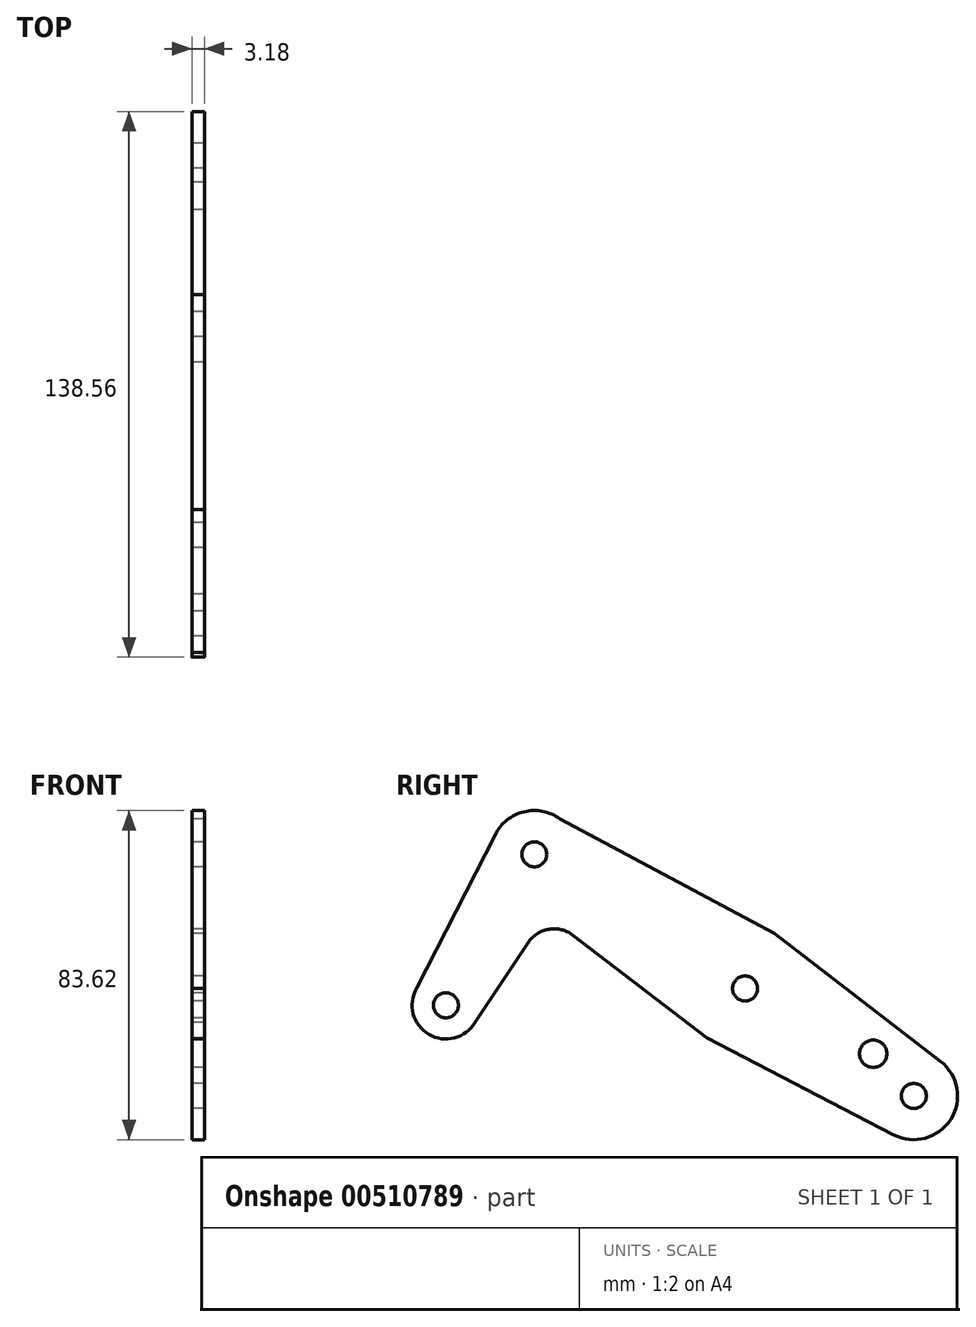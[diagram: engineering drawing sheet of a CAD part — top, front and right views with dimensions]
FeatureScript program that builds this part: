
annotation { "Feature Type Name" : "Feature", "Feature Type Description" : "" }
export const myFeature = defineFeature(function(context is Context, id is Id, definition is map)
    precondition{}
    {
        {
            var Q0;
            Q0=qCreatedBy(makeId("Right.planeOp"),FACE);
            var sketch = newSketch(context, id + "F0", { "sketchPlane" : qUnion([Q0])});
            skCircle(sketch, "E0", {"center": v(-33.05, 6.2) * mm, "radius": 3.18 * mm});
            skCircle(sketch, "E1", {"center": v(-10.58, 44.56) * mm, "radius": 3.18 * mm});
            skCircle(sketch, "E2", {"center": v(42.98, 10.45) * mm, "radius": 3.18 * mm});
            skCircle(sketch, "E3", {"center": v(85.83, -16.84) * mm, "radius": 3.18 * mm});
            skArc(sketch, "E4", {"start": v(-40.45, 10.52) * mm, "mid": v(-37.38, -1.2) * mm, "end": v(-25.66, 1.86) * mm});
            skArc(sketch, "E5", {"start": v(80.72, -26.7) * mm, "mid": v(95.2, -22.81) * mm, "end": v(92.61, -8.04) * mm});
            skArc(sketch, "E6", {"start": v(33.31, -2.15) * mm, "mid": v(35.67, -3.65) * mm, "end": v(38.26, -4.71) * mm});
            skArc(sketch, "E7", {"start": v(-4.1, 53.58) * mm, "mid": v(-13.2, 55.36) * mm, "end": v(-20.48, 49.61) * mm});
            skCircle(sketch, "E8", {"center": v(75.53, -6.12) * mm, "radius": 3.48 * mm});
            skLineSegment(sketch, "E9", {"start": v(-40.45, 10.52) * mm, "end": v(-20.48, 49.61) * mm});
            skLineSegment(sketch, "E10", {"start": v(-25.66, 1.86) * mm, "end": v(-12.2, 22.08) * mm});
            skLineSegment(sketch, "E11", {"start": v(-4.1, 53.58) * mm, "end": v(50.45, 24.45) * mm});
            skLineSegment(sketch, "E12", {"start": v(50.45, 24.45) * mm, "end": v(92.61, -8.04) * mm});
            skLineSegment(sketch, "E13", {"start": v(-0.74, 23.98) * mm, "end": v(33.31, -2.15) * mm});
            skLineSegment(sketch, "E14", {"start": v(33.31, -2.15) * mm, "end": v(80.72, -26.7) * mm});
            skPoint(sketch, "E15.visualSharp", {"position": v(-7.48, 29.16) * mm});
            skArc(sketch, "E15.filletArc", {"start": v(-0.74, 23.98) * mm, "mid": v(-6.88, 25.52) * mm, "end": v(-12.2, 22.08) * mm});
            skArc(sketch, "E16.trimOffspring", {"start": v(54.62, 21.25) * mm, "mid": v(52.67, 23.02) * mm, "end": v(50.45, 24.45) * mm});
            skSolve(sketch);
        }
        {
            var Q0;
            Q0=makeQuery(id+"F0.imprint","IMPRINT",FACE,{"disambiguationData":[TD([[makeQuery(id+"F0.imprint","IMPRINT",EDGE,{"derivedFrom":sQuery(id+"F0.wireOp",EDGE,"E0")}),-1.0]])]});
            extrude(context, id + "F1", {"entities" : qUnion([Q0]), "depth" : 3.17 * mm, "offsetDistance" : 25.4 * mm});
        }
    });
